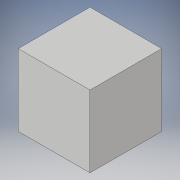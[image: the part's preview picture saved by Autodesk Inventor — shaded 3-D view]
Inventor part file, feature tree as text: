
AUTODESK INVENTOR PART (.ipt)
format: ipt  version: 2018 (Build 220112000, 112)  size: 83,968 bytes
history: native  units: in
note: dims shown in document units (in); Inventor stores cm internally (conversion verified against a paired STEP export)
features: extrude x1, sketch x1
ambient origin geometry x8: Origin, YZ Plane, XZ Plane, XY Plane, X Axis, Y Axis, Z Axis, Center Point
bodies: Solid1 (feature_tree)
feature tree (2):
  extrude  "Extrusion1"  Depth=1.0in
  sketch  "Sketch1"  dims[d0=1.0in d1=1.0in d2=1.0in d3=0.0in]
